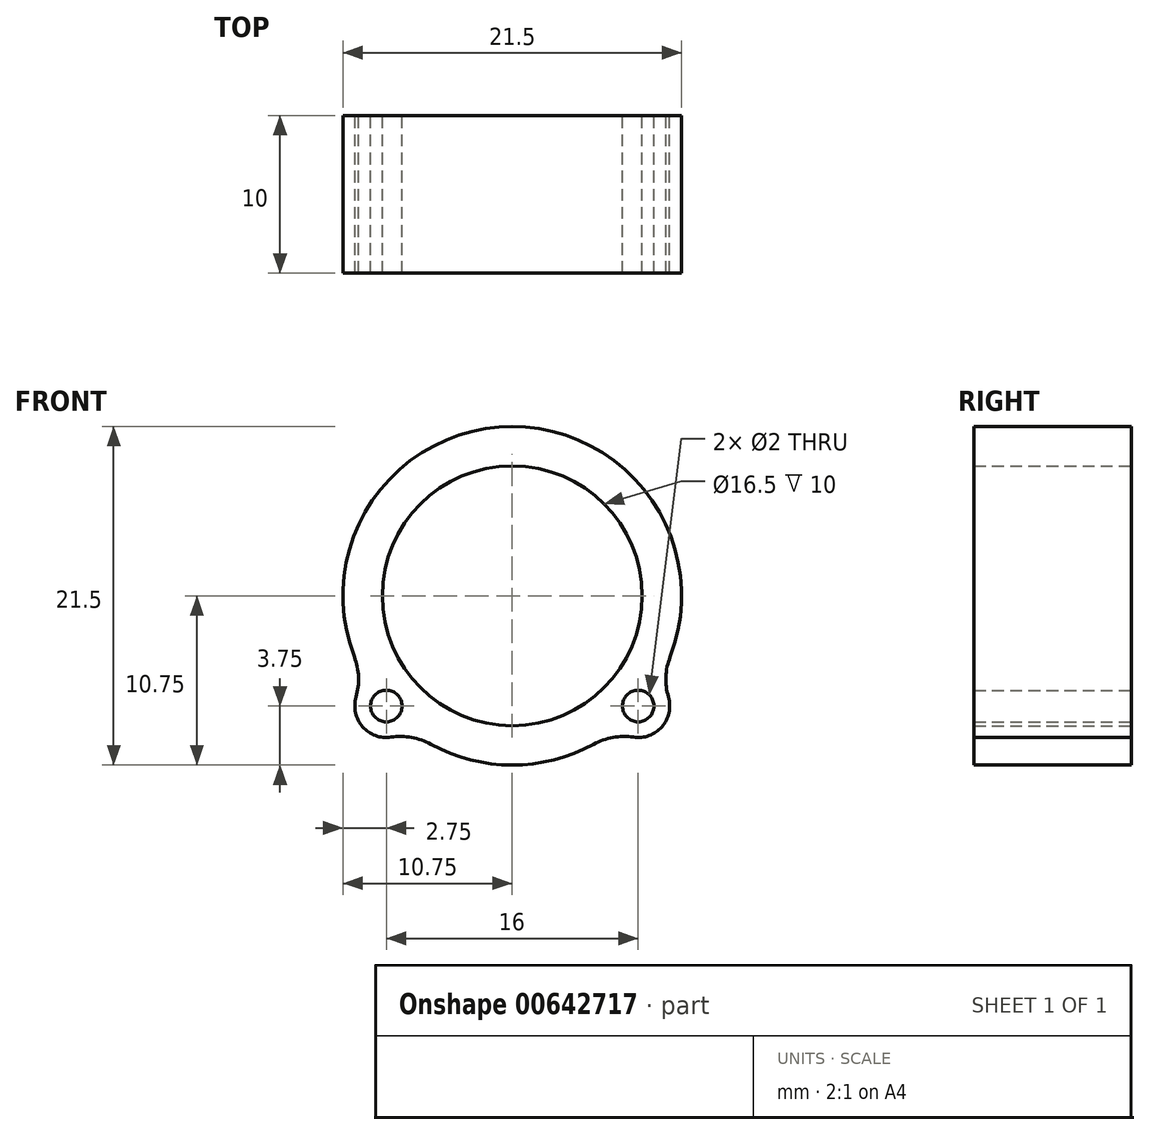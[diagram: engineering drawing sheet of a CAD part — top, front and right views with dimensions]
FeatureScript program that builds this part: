
annotation { "Feature Type Name" : "Feature", "Feature Type Description" : "" }
export const myFeature = defineFeature(function(context is Context, id is Id, definition is map)
    precondition{}
    {
        {
            var Q0;
            Q0=qCreatedBy(makeId("Front.planeOp"),FACE);
            var sketch = newSketch(context, id + "F0", { "sketchPlane" : qUnion([Q0])});
            skCircle(sketch, "E0", {"center": v(0, 0) * mm, "radius": 8.25 * mm});
            skPoint(sketch, "E1.orphan", {"position": v(7, -7) * mm});
            skPoint(sketch, "E2.orphan", {"position": v(-12.24, -4.39) * mm});
            skPoint(sketch, "E3.start.orphan", {"position": v(-4.37, -7) * mm});
            skCircle(sketch, "E4", {"center": v(-8, -7) * mm, "radius": 1 * mm});
            skCircle(sketch, "E5", {"center": v(8, -7) * mm, "radius": 1 * mm});
            skPoint(sketch, "E6.visualSharp", {"position": v(13.18, -3) * mm});
            skPoint(sketch, "E7.visualSharp", {"position": v(11.8, -7.54) * mm});
            skPoint(sketch, "E8.visualSharp", {"position": v(-12.65, -3.07) * mm});
            skPoint(sketch, "E9.visualSharp", {"position": v(-11.43, -7.23) * mm});
            skArc(sketch, "E10", {"start": v(-5.17, -9.42) * mm, "mid": v(0, -10.75) * mm, "end": v(5.17, -9.42) * mm});
            skArc(sketch, "E11", {"start": v(-9.92, -6.44) * mm, "mid": v(-9.5, -8.32) * mm, "end": v(-7.7, -8.98) * mm});
            skArc(sketch, "E12", {"start": v(7.7, -8.98) * mm, "mid": v(9.5, -8.32) * mm, "end": v(9.92, -6.44) * mm});
            skArc(sketch, "E13.trimOffspring", {"start": v(10.03, -3.87) * mm, "mid": v(0, 10.75) * mm, "end": v(-10.03, -3.87) * mm});
            skPoint(sketch, "E14.visualSharp", {"position": v(-9.27, -5.45) * mm});
            skArc(sketch, "E14.filletArc", {"start": v(-9.92, -6.44) * mm, "mid": v(-9.76, -5.15) * mm, "end": v(-10.03, -3.87) * mm});
            skPoint(sketch, "E15.visualSharp", {"position": v(-6.63, -8.46) * mm});
            skArc(sketch, "E15.filletArc", {"start": v(-5.17, -9.42) * mm, "mid": v(-6.4, -9) * mm, "end": v(-7.7, -8.98) * mm});
            skPoint(sketch, "E16.visualSharp", {"position": v(6.63, -8.46) * mm});
            skArc(sketch, "E16.filletArc", {"start": v(7.7, -8.98) * mm, "mid": v(6.4, -9) * mm, "end": v(5.17, -9.42) * mm});
            skPoint(sketch, "E17.visualSharp", {"position": v(9.27, -5.45) * mm});
            skArc(sketch, "E17.filletArc", {"start": v(10.03, -3.87) * mm, "mid": v(9.76, -5.15) * mm, "end": v(9.92, -6.44) * mm});
            skSolve(sketch);
        }
        {
            var Q0;
            Q0=makeQuery(id+"F0.imprint","IMPRINT",FACE,{"disambiguationData":[TD([[makeQuery(id+"F0.imprint","IMPRINT",EDGE,{"derivedFrom":sQuery(id+"F0.wireOp",EDGE,"E0")}),-1.0]])]});
            extrude(context, id + "F1", {"entities" : qUnion([Q0]), "depth" : 10 * mm, "offsetDistance" : 25 * mm});
        }
    });
